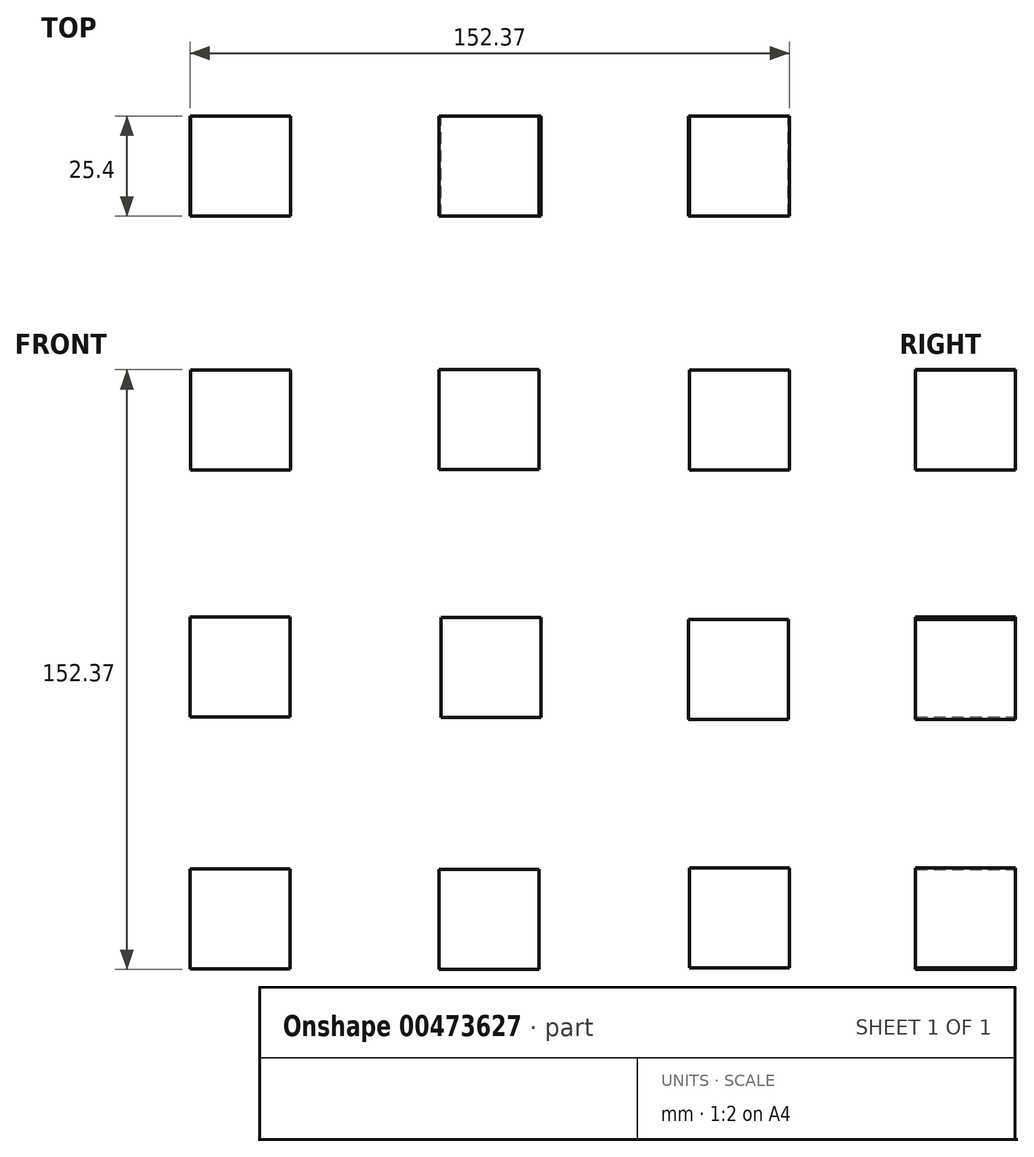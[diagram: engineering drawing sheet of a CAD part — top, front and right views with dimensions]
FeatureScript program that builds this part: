
annotation { "Feature Type Name" : "Feature", "Feature Type Description" : "" }
export const myFeature = defineFeature(function(context is Context, id is Id, definition is map)
    precondition{}
    {
        {
            var Q0;
            Q0=qCreatedBy(makeId("Front.planeOp"),FACE);
            var sketch = newSketch(context, id + "F0", { "sketchPlane" : qUnion([Q0])});
            skLineSegment(sketch, "E0", {"start": v(-75.93, 75.93) * mm, "end": v(-75.93, 50.53) * mm});
            skLineSegment(sketch, "E1", {"start": v(-75.93, 50.53) * mm, "end": v(-50.53, 50.53) * mm});
            skLineSegment(sketch, "E2", {"start": v(-50.53, 50.53) * mm, "end": v(-50.53, 75.93) * mm});
            skLineSegment(sketch, "E3", {"start": v(-50.53, 75.93) * mm, "end": v(-75.93, 75.93) * mm});
            skSolve(sketch);
        }
        {
            var Q0;
            Q0=qCreatedBy(makeId("Front.planeOp"),FACE);
            var sketch = newSketch(context, id + "F1", { "sketchPlane" : qUnion([Q0])});
            skLineSegment(sketch, "E4", {"start": v(-76.1, -50.72) * mm, "end": v(-76.1, -76.12) * mm});
            skLineSegment(sketch, "E5", {"start": v(-76.1, -76.12) * mm, "end": v(-50.7, -76.12) * mm});
            skLineSegment(sketch, "E6", {"start": v(-50.7, -76.12) * mm, "end": v(-50.7, -50.72) * mm});
            skLineSegment(sketch, "E7", {"start": v(-50.7, -50.72) * mm, "end": v(-76.1, -50.72) * mm});
            skSolve(sketch);
        }
        {
            var Q0;
            Q0=qCreatedBy(makeId("Front.planeOp"),FACE);
            var sketch = newSketch(context, id + "F2", { "sketchPlane" : qUnion([Q0])});
            skLineSegment(sketch, "E8", {"start": v(-12.77, 76.1) * mm, "end": v(-12.77, 50.7) * mm});
            skLineSegment(sketch, "E9", {"start": v(-12.77, 50.7) * mm, "end": v(12.63, 50.7) * mm});
            skLineSegment(sketch, "E10", {"start": v(12.63, 50.7) * mm, "end": v(12.63, 76.1) * mm});
            skLineSegment(sketch, "E11", {"start": v(12.63, 76.1) * mm, "end": v(-12.77, 76.1) * mm});
            skSolve(sketch);
        }
        {
            var Q0;
            Q0=qCreatedBy(makeId("Front.planeOp"),FACE);
            var sketch = newSketch(context, id + "F3", { "sketchPlane" : qUnion([Q0])});
            skLineSegment(sketch, "E12", {"start": v(-12.77, -50.88) * mm, "end": v(-12.77, -76.28) * mm});
            skLineSegment(sketch, "E13", {"start": v(-12.77, -76.28) * mm, "end": v(12.63, -76.28) * mm});
            skLineSegment(sketch, "E14", {"start": v(12.63, -76.28) * mm, "end": v(12.63, -50.88) * mm});
            skLineSegment(sketch, "E15", {"start": v(12.63, -50.88) * mm, "end": v(-12.77, -50.88) * mm});
            skSolve(sketch);
        }
        {
            var Q0;
            Q0=qCreatedBy(makeId("Front.planeOp"),FACE);
            var sketch = newSketch(context, id + "F4", { "sketchPlane" : qUnion([Q0])});
            skLineSegment(sketch, "E16", {"start": v(-76.1, 13.25) * mm, "end": v(-76.1, -12.15) * mm});
            skLineSegment(sketch, "E17", {"start": v(-76.1, -12.15) * mm, "end": v(-50.7, -12.15) * mm});
            skLineSegment(sketch, "E18", {"start": v(-50.7, -12.15) * mm, "end": v(-50.7, 13.25) * mm});
            skLineSegment(sketch, "E19", {"start": v(-50.7, 13.25) * mm, "end": v(-76.1, 13.25) * mm});
            skSolve(sketch);
        }
        {
            var Q0;
            Q0=qCreatedBy(makeId("Front.planeOp"),FACE);
            var sketch = newSketch(context, id + "F5", { "sketchPlane" : qUnion([Q0])});
            skLineSegment(sketch, "E20", {"start": v(-12.28, 13.1) * mm, "end": v(-12.28, -12.3) * mm});
            skLineSegment(sketch, "E21", {"start": v(-12.28, -12.3) * mm, "end": v(13.12, -12.3) * mm});
            skLineSegment(sketch, "E22", {"start": v(13.12, -12.3) * mm, "end": v(13.12, 13.1) * mm});
            skLineSegment(sketch, "E23", {"start": v(13.12, 13.1) * mm, "end": v(-12.28, 13.1) * mm});
            skSolve(sketch);
        }
        {
            var Q0;
            Q0=qCreatedBy(makeId("Front.planeOp"),FACE);
            var sketch = newSketch(context, id + "F6", { "sketchPlane" : qUnion([Q0])});
            skLineSegment(sketch, "E24", {"start": v(50.88, 75.96) * mm, "end": v(50.88, 50.56) * mm});
            skLineSegment(sketch, "E25", {"start": v(50.88, 50.56) * mm, "end": v(76.28, 50.56) * mm});
            skLineSegment(sketch, "E26", {"start": v(76.28, 50.56) * mm, "end": v(76.28, 75.96) * mm});
            skLineSegment(sketch, "E27", {"start": v(76.28, 75.96) * mm, "end": v(50.88, 75.96) * mm});
            skSolve(sketch);
        }
        {
            var Q0;
            Q0=qCreatedBy(makeId("Front.planeOp"),FACE);
            var sketch = newSketch(context, id + "F7", { "sketchPlane" : qUnion([Q0])});
            skLineSegment(sketch, "E28", {"start": v(50.86, -50.56) * mm, "end": v(50.86, -75.96) * mm});
            skLineSegment(sketch, "E29", {"start": v(50.86, -75.96) * mm, "end": v(76.26, -75.96) * mm});
            skLineSegment(sketch, "E30", {"start": v(76.26, -75.96) * mm, "end": v(76.26, -50.56) * mm});
            skLineSegment(sketch, "E31", {"start": v(76.26, -50.56) * mm, "end": v(50.86, -50.56) * mm});
            skSolve(sketch);
        }
        {
            var Q0;
            Q0=qCreatedBy(makeId("Front.planeOp"),FACE);
            var sketch = newSketch(context, id + "F8", { "sketchPlane" : qUnion([Q0])});
            skLineSegment(sketch, "E32", {"start": v(50.56, 12.6) * mm, "end": v(50.56, -12.8) * mm});
            skLineSegment(sketch, "E33", {"start": v(50.56, -12.8) * mm, "end": v(75.96, -12.8) * mm});
            skLineSegment(sketch, "E34", {"start": v(75.96, -12.8) * mm, "end": v(75.96, 12.6) * mm});
            skLineSegment(sketch, "E35", {"start": v(75.96, 12.6) * mm, "end": v(50.56, 12.6) * mm});
            skSolve(sketch);
        }
        {
            var Q0;
            Q0=makeQuery(id+"F0.imprint","IMPRINT",FACE,{"disambiguationData":[TD([[makeQuery(id+"F0.imprint","IMPRINT",EDGE,{"derivedFrom":sQuery(id+"F0.wireOp",EDGE,"E0")}),1.0]])]});
            var Q1;
            Q1=makeQuery(id+"F1.imprint","IMPRINT",FACE,{"disambiguationData":[TD([[makeQuery(id+"F1.imprint","IMPRINT",EDGE,{"derivedFrom":sQuery(id+"F1.wireOp",EDGE,"E4")}),1.0]])]});
            var Q2;
            Q2=makeQuery(id+"F2.imprint","IMPRINT",FACE,{"disambiguationData":[TD([[makeQuery(id+"F2.imprint","IMPRINT",EDGE,{"derivedFrom":sQuery(id+"F2.wireOp",EDGE,"E8")}),1.0]])]});
            var Q3;
            Q3=makeQuery(id+"F3.imprint","IMPRINT",FACE,{"disambiguationData":[TD([[makeQuery(id+"F3.imprint","IMPRINT",EDGE,{"derivedFrom":sQuery(id+"F3.wireOp",EDGE,"E12")}),1.0]])]});
            var Q4;
            Q4=makeQuery(id+"F4.imprint","IMPRINT",FACE,{"disambiguationData":[TD([[makeQuery(id+"F4.imprint","IMPRINT",EDGE,{"derivedFrom":sQuery(id+"F4.wireOp",EDGE,"E16")}),1.0]])]});
            var Q5;
            Q5=makeQuery(id+"F8.imprint","IMPRINT",FACE,{"disambiguationData":[TD([[makeQuery(id+"F8.imprint","IMPRINT",EDGE,{"derivedFrom":sQuery(id+"F8.wireOp",EDGE,"E32")}),1.0]])]});
            var Q6;
            Q6=makeQuery(id+"F6.imprint","IMPRINT",FACE,{"disambiguationData":[TD([[makeQuery(id+"F6.imprint","IMPRINT",EDGE,{"derivedFrom":sQuery(id+"F6.wireOp",EDGE,"E24")}),1.0]])]});
            var Q7;
            Q7=makeQuery(id+"F5.imprint","IMPRINT",FACE,{"disambiguationData":[TD([[makeQuery(id+"F5.imprint","IMPRINT",EDGE,{"derivedFrom":sQuery(id+"F5.wireOp",EDGE,"E20")}),1.0]])]});
            var Q8;
            Q8=makeQuery(id+"F7.imprint","IMPRINT",FACE,{"disambiguationData":[TD([[makeQuery(id+"F7.imprint","IMPRINT",EDGE,{"derivedFrom":sQuery(id+"F7.wireOp",EDGE,"E28")}),1.0]])]});
            extrude(context, id + "F9", {"entities" : qUnion([Q0, Q1, Q2, Q3, Q4, Q5, Q6, Q7, Q8]), "depth" : 25.4 * mm});
        }
    });
